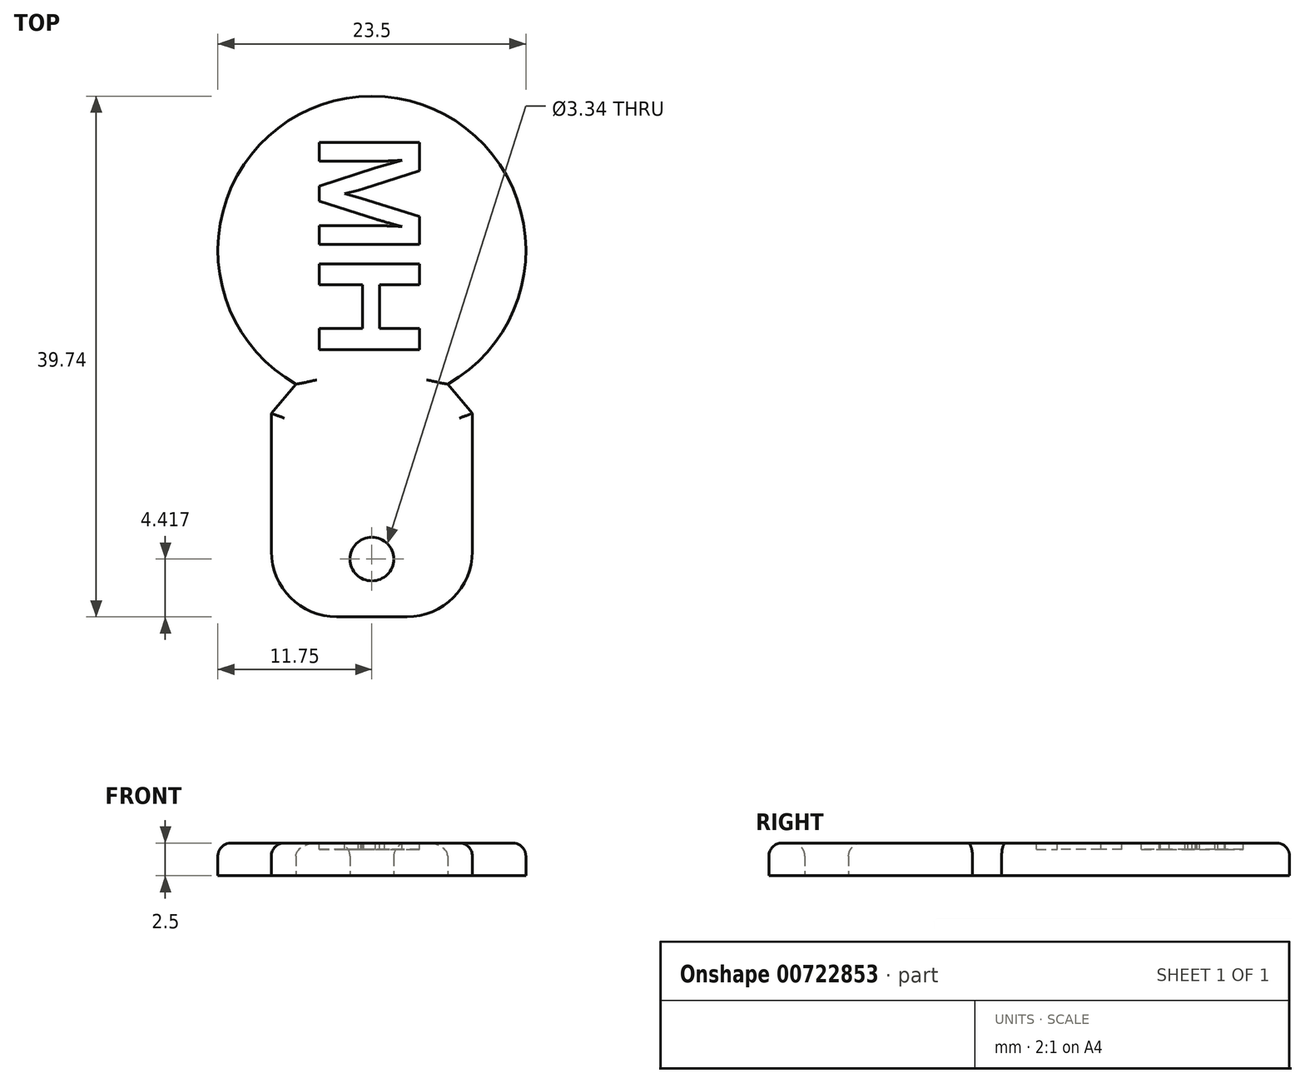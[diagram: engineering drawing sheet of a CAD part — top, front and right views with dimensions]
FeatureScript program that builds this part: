
annotation { "Feature Type Name" : "Feature", "Feature Type Description" : "" }
export const myFeature = defineFeature(function(context is Context, id is Id, definition is map)
    precondition{}
    {
        {
            var Q0;
            Q0=qCreatedBy(makeId("Top.planeOp"),FACE);
            var sketch = newSketch(context, id + "F0", { "sketchPlane" : qUnion([Q0])});
            skCircle(sketch, "E0", {"center": v(0, 27.99) * mm, "radius": 11.75 * mm});
            skLineSegment(sketch, "E1", {"start": v(-5.78, 17.76) * mm, "end": v(-7.67, 15.54) * mm});
            skLineSegment(sketch, "E2", {"start": v(-7.67, 15.54) * mm, "end": v(-7.67, 0) * mm});
            skLineSegment(sketch, "E3", {"start": v(-7.67, 0) * mm, "end": v(0, 0) * mm});
            skLineSegment(sketch, "E4", {"start": v(0, 0) * mm, "end": v(0, 16.24) * mm});
            skLineSegment(sketch, "E5.MirrorCS", {"start": v(7.67, 15.54) * mm, "end": v(7.67, 0) * mm});
            skLineSegment(sketch, "E6.MirrorCS", {"start": v(5.78, 17.76) * mm, "end": v(7.67, 15.54) * mm});
            skLineSegment(sketch, "E7.MirrorCS", {"start": v(7.67, 0) * mm, "end": v(0, 0) * mm});
            skCircle(sketch, "E8", {"center": v(0, 4.42) * mm, "radius": 1.67 * mm});
            skSolve(sketch);
        }
        {
            var Q0;
            Q0 = qSketchRegion(id + "F0", true);
            extrude(context, id + "F1", {"entities" : qUnion([Q0]), "depth" : 2.5 * mm, "offsetDistance" : 25 * mm});
        }
        {
            var Q0;
            Q0=makeQuery(id+"F1.opExtrude","SWEPT_EDGE",EDGE,{"disambiguationData":[OSD([sQuery(id+"F0.wireOp",EDGE,"E5.MirrorCS"),sQuery(id+"F0.wireOp",EDGE,"E7.MirrorCS")])]});
            var Q1;
            Q1=makeQuery(id+"F1.opExtrude","SWEPT_EDGE",EDGE,{"disambiguationData":[OSD([sQuery(id+"F0.wireOp",EDGE,"E2"),sQuery(id+"F0.wireOp",EDGE,"E3")])]});
            fillet(context, id + "F2", {"entities" : qUnion([Q0, Q1]), "radius" : 5 * mm, "tangentPropagation" : true, "allowEdgeOverflow" : false});
        }
        {
            var Q0;
            Q0=makeQuery(id+"F1.opExtrude","CAP_FACE",FACE,{"disambiguationData":[OSD([sQuery(id+"F0.wireOp",EDGE,"E0"),sQuery(id+"F0.wireOp",EDGE,"E1"),sQuery(id+"F0.wireOp",EDGE,"E2"),sQuery(id+"F0.wireOp",EDGE,"E3"),sQuery(id+"F0.wireOp",EDGE,"E5.MirrorCS"),sQuery(id+"F0.wireOp",EDGE,"E6.MirrorCS"),sQuery(id+"F0.wireOp",EDGE,"E7.MirrorCS"),sQuery(id+"F0.wireOp",EDGE,"E8")])],"isStart":false});
            fillet(context, id + "F3", {"entities" : qUnion([Q0]), "radius" : 1 * mm, "tangentPropagation" : true, "allowEdgeOverflow" : false});
        }
        {
            var Q0;
            Q0=makeQuery(id+"F1.opExtrude","CAP_FACE",FACE,{"disambiguationData":[OSD([sQuery(id+"F0.wireOp",EDGE,"E0"),sQuery(id+"F0.wireOp",EDGE,"E1"),sQuery(id+"F0.wireOp",EDGE,"E2"),sQuery(id+"F0.wireOp",EDGE,"E3"),sQuery(id+"F0.wireOp",EDGE,"E5.MirrorCS"),sQuery(id+"F0.wireOp",EDGE,"E6.MirrorCS"),sQuery(id+"F0.wireOp",EDGE,"E7.MirrorCS"),sQuery(id+"F0.wireOp",EDGE,"E8")])],"isStart":false});
            var sketch = newSketch(context, id + "F4", { "sketchPlane" : qUnion([Q0])});
            skText(sketch, "E9", { "text": "MH", "fontName": "Arimo-Bold.ttf"});
            const initialGuessF4  = {"E9": [-0.004, 0.03694, 0, -1, 0.008]};
            skSetInitialGuess(sketch, initialGuessF4);
            skSolve(sketch);
        }
        {
            var Q0;
            Q0 = qSketchRegion(id + "F4", true);
            extrude(context, id + "F5", {"entities" : qUnion([Q0]), "operationType" : NewBodyOperationType.REMOVE, "oppositeDirection" : true, "depth" : 0.5 * mm, "offsetDistance" : 25 * mm});
        }
    });
